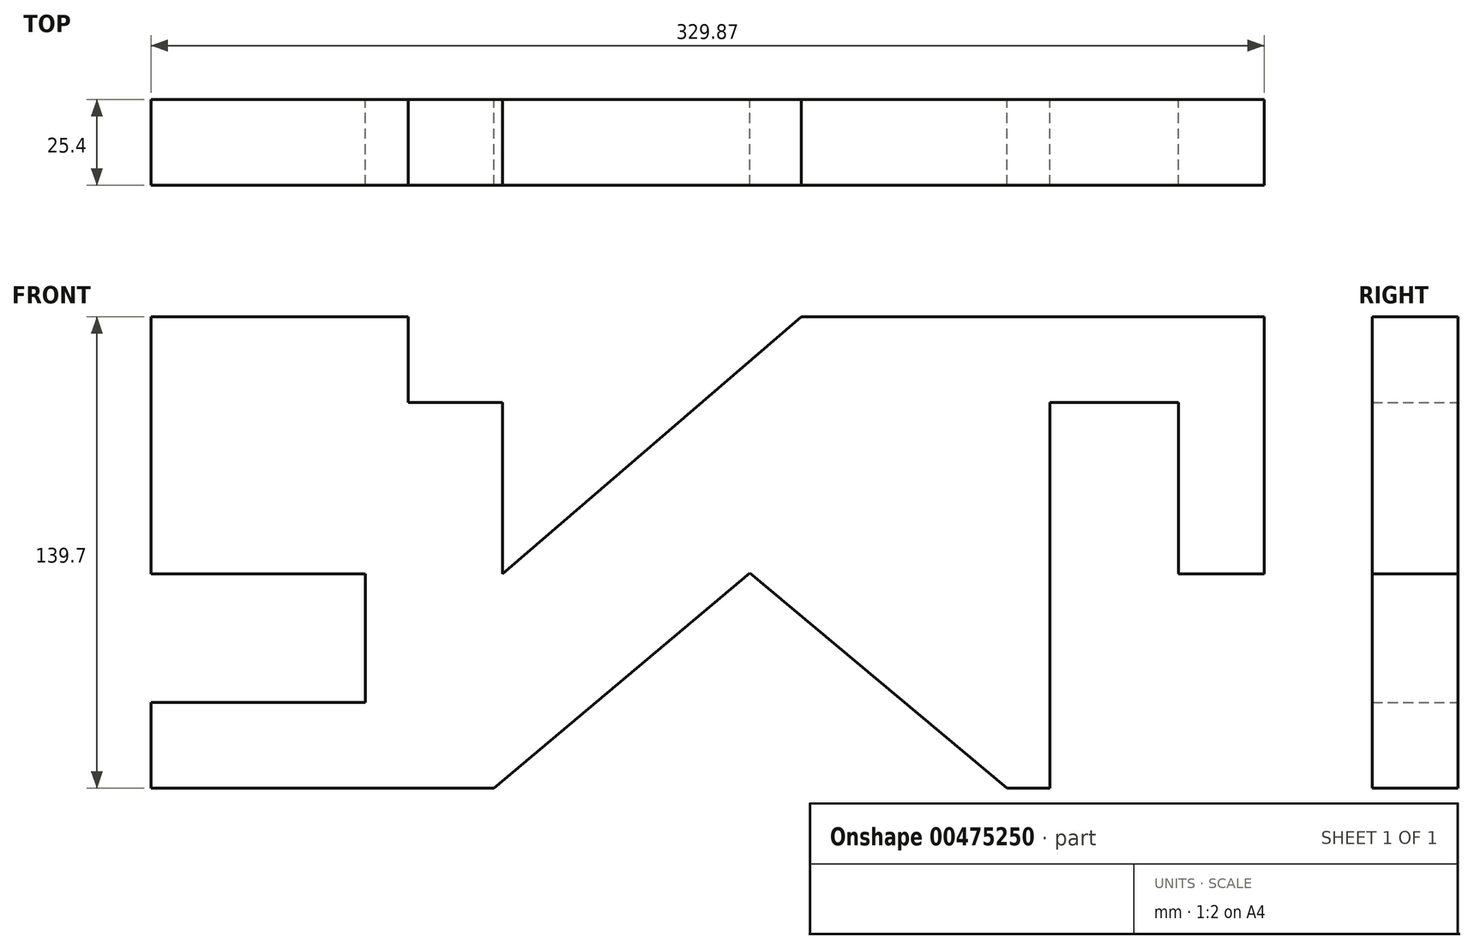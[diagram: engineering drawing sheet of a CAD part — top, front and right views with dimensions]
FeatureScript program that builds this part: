
annotation { "Feature Type Name" : "Feature", "Feature Type Description" : "" }
export const myFeature = defineFeature(function(context is Context, id is Id, definition is map)
    precondition{}
    {
        {
            var Q0;
            Q0=qCreatedBy(makeId("Front.planeOp"),FACE);
            var sketch = newSketch(context, id + "F0", { "sketchPlane" : qUnion([Q0])});
            skLineSegment(sketch, "E0", {"start": v(0, 0) * mm, "end": v(76.2, 0) * mm});
            skLineSegment(sketch, "E1", {"start": v(76.2, 0) * mm, "end": v(76.2, -25.4) * mm});
            skLineSegment(sketch, "E2", {"start": v(76.2, -25.4) * mm, "end": v(104.14, -25.4) * mm});
            skLineSegment(sketch, "E3", {"start": v(104.14, -25.4) * mm, "end": v(104.14, -76.2) * mm});
            skLineSegment(sketch, "E4", {"start": v(104.14, -76.2) * mm, "end": v(192.71, 0) * mm});
            skLineSegment(sketch, "E5", {"start": v(192.71, 0) * mm, "end": v(329.87, 0) * mm});
            skLineSegment(sketch, "E6", {"start": v(329.87, 0) * mm, "end": v(329.87, -76.2) * mm});
            skLineSegment(sketch, "E7", {"start": v(329.87, -76.2) * mm, "end": v(304.47, -76.2) * mm});
            skLineSegment(sketch, "E8", {"start": v(304.47, -76.2) * mm, "end": v(304.47, -25.4) * mm});
            skLineSegment(sketch, "E9", {"start": v(304.47, -25.4) * mm, "end": v(266.37, -25.4) * mm});
            skLineSegment(sketch, "E10", {"start": v(0, 0) * mm, "end": v(0, -76.2) * mm});
            skLineSegment(sketch, "E11", {"start": v(0, -76.2) * mm, "end": v(63.5, -76.2) * mm});
            skLineSegment(sketch, "E12", {"start": v(63.5, -76.2) * mm, "end": v(63.5, -114.3) * mm});
            skLineSegment(sketch, "E13", {"start": v(63.5, -114.3) * mm, "end": v(0, -114.3) * mm});
            skLineSegment(sketch, "E14", {"start": v(0, -114.3) * mm, "end": v(0, -139.7) * mm});
            skLineSegment(sketch, "E15", {"start": v(0, -139.7) * mm, "end": v(101.6, -139.7) * mm});
            skLineSegment(sketch, "E16", {"start": v(266.37, -25.4) * mm, "end": v(266.37, -139.7) * mm});
            skLineSegment(sketch, "E17", {"start": v(177.51, -75.9) * mm, "end": v(101.6, -139.7) * mm});
            skLineSegment(sketch, "E18", {"start": v(266.37, -139.7) * mm, "end": v(253.67, -139.7) * mm});
            skLineSegment(sketch, "E19", {"start": v(253.67, -139.7) * mm, "end": v(177.51, -75.9) * mm});
            skSolve(sketch);
        }
        {
            var Q0;
            Q0=makeQuery(id+"F0.imprint","IMPRINT",FACE,{"disambiguationData":[TD([[makeQuery(id+"F0.imprint","IMPRINT",EDGE,{"derivedFrom":sQuery(id+"F0.wireOp",EDGE,"E0")}),-1.0]])]});
            extrude(context, id + "F1", {"entities" : qUnion([Q0]), "depth" : 25.4 * mm});
        }
    });
